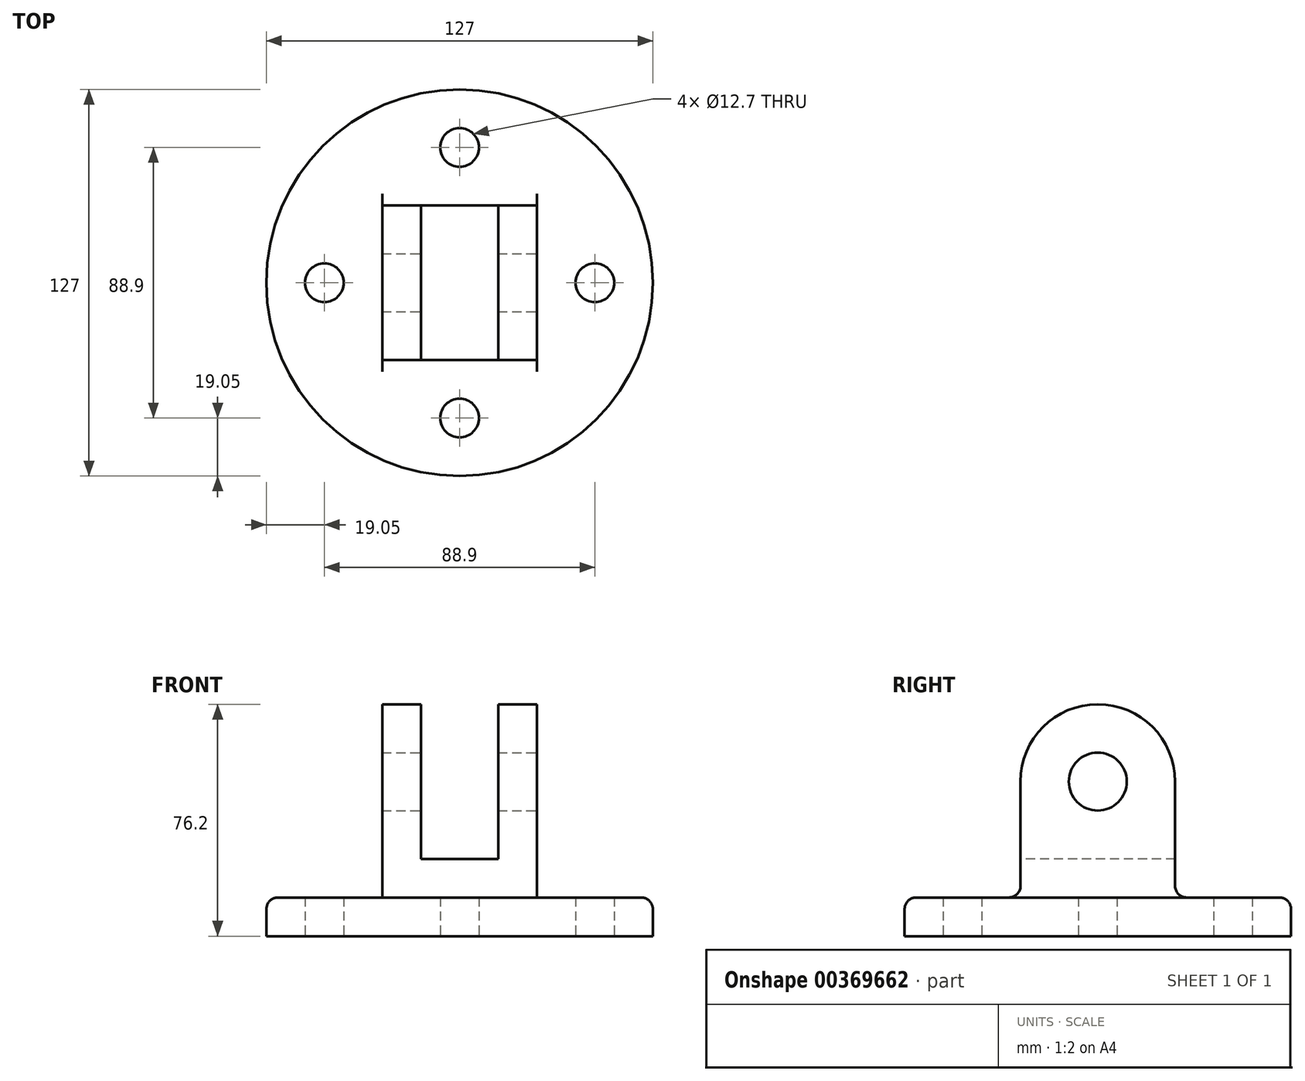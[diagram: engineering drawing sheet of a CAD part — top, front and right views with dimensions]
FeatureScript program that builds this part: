
annotation { "Feature Type Name" : "Feature", "Feature Type Description" : "" }
export const myFeature = defineFeature(function(context is Context, id is Id, definition is map)
    precondition{}
    {
        {
            var Q0;
            Q0=qCreatedBy(makeId("Top.planeOp"),FACE);
            var sketch = newSketch(context, id + "F0", { "sketchPlane" : qUnion([Q0])});
            skCircle(sketch, "E0", {"center": v(0, 0) * mm, "radius": 63.5 * mm});
            skCircle(sketch, "E1", {"center": v(0, 0) * mm, "radius": 44.45 * mm, "construction": true});
            skCircle(sketch, "E2", {"center": v(0, 44.45) * mm, "radius": 6.35 * mm});
            skCircle(sketch, "E3", {"center": v(44.45, 0) * mm, "radius": 6.35 * mm});
            skCircle(sketch, "E4", {"center": v(0, -44.45) * mm, "radius": 6.35 * mm});
            skCircle(sketch, "E5", {"center": v(-44.45, 0) * mm, "radius": 6.35 * mm});
            skLineSegment(sketch, "E6", {"start": v(-25.4, 25.4) * mm, "end": v(-25.4, -25.4) * mm});
            skLineSegment(sketch, "E7", {"start": v(-25.4, -25.4) * mm, "end": v(25.4, -25.4) * mm});
            skLineSegment(sketch, "E8", {"start": v(25.4, -25.4) * mm, "end": v(25.4, 25.4) * mm});
            skLineSegment(sketch, "E9", {"start": v(25.4, 25.4) * mm, "end": v(-25.4, 25.4) * mm});
            skLineSegment(sketch, "E10", {"start": v(-12.7, 25.4) * mm, "end": v(-12.7, -25.4) * mm});
            skLineSegment(sketch, "E11", {"start": v(12.7, 25.4) * mm, "end": v(12.7, -25.4) * mm});
            skSolve(sketch);
        }
        {
            var Q0;
            Q0=makeQuery(id+"F0.imprint","IMPRINT",FACE,{"disambiguationData":[TD([[makeQuery(id+"F0.imprint","IMPRINT",EDGE,{"derivedFrom":sQuery(id+"F0.wireOp",EDGE,"E0")}),1.0]])]});
            extrude(context, id + "F1", {"entities" : qUnion([Q0]), "depth" : 12.7 * mm});
        }
        {
            var Q0;
            {var subQ0=sQuery(id+"F0.wireOp",EDGE,"E6");Q0=makeQuery(id+"F0.imprint","IMPRINT",FACE,{"disambiguationData":[TD([[makeQuery(id+"F0.imprint","IMPRINT",EDGE,{"derivedFrom":subQ0}),1.0]])]});}
            var Q1;
            {var subQ0=sQuery(id+"F0.wireOp",EDGE,"E8");Q1=makeQuery(id+"F0.imprint","IMPRINT",FACE,{"disambiguationData":[TD([[makeQuery(id+"F0.imprint","IMPRINT",EDGE,{"derivedFrom":subQ0}),1.0]])]});}
            extrude(context, id + "F2", {"entities" : qUnion([Q0, Q1]), "operationType" : NewBodyOperationType.ADD, "depth" : 76.2 * mm});
        }
        {
            var Q0;
            {var subQ0=sQuery(id+"F0.wireOp",EDGE,"E10");Q0=makeQuery(id+"F0.imprint","IMPRINT",FACE,{"disambiguationData":[TD([[makeQuery(id+"F0.imprint","IMPRINT",EDGE,{"derivedFrom":subQ0}),1.0]])]});}
            extrude(context, id + "F3", {"entities" : qUnion([Q0]), "operationType" : NewBodyOperationType.ADD, "depth" : 25.4 * mm});
        }
        {
            var Q0;
            Q0=makeQuery(id+"F2.opExtrude","SWEPT_FACE",FACE,{"disambiguationData":[OSD([sQuery(id+"F0.wireOp",EDGE,"E8")])]});
            var sketch = newSketch(context, id + "F4", { "sketchPlane" : qUnion([Q0])});
            skLineSegment(sketch, "E12", {"start": v(0, 0) * mm, "end": v(0, 50.8) * mm, "construction": true});
            skPoint(sketch, "E12.endSnap0", {"position": v(0, 76.2) * mm});
            skCircle(sketch, "E13", {"center": v(0, 50.8) * mm, "radius": 9.53 * mm});
            skArc(sketch, "E14", {"start": v(25.4, 50.8) * mm, "mid": v(0, 76.2) * mm, "end": v(-25.4, 50.8) * mm});
            skLineSegment(sketch, "E15", {"start": v(-25.4, 12.7) * mm, "end": v(-25.4, 50.8) * mm});
            skLineSegment(sketch, "E16", {"start": v(25.4, 50.8) * mm, "end": v(25.4, 12.7) * mm});
            skLineSegment(sketch, "E17", {"start": v(-25.4, 76.2) * mm, "end": v(25.4, 76.2) * mm});
            skLineSegment(sketch, "E18", {"start": v(25.4, 76.2) * mm, "end": v(25.4, 50.8) * mm});
            skLineSegment(sketch, "E19", {"start": v(-25.4, 76.2) * mm, "end": v(-25.4, 50.8) * mm});
            skSolve(sketch);
        }
        {
            var Q0;
            Q0 = qSketchRegion(id + "F4", true);
            extrude(context, id + "F5", {"entities" : qUnion([Q0]), "operationType" : NewBodyOperationType.REMOVE, "endBound" : BoundingType.THROUGH_ALL, "oppositeDirection" : true, "depth" : 25.4 * mm});
        }
        {
            var Q0;
            Q0=makeQuery(id+"F1.opExtrude","CAP_EDGE",EDGE,{"disambiguationData":[OSD([sQuery(id+"F0.wireOp",EDGE,"E8")])],"isStart":false});
            var Q1;
            {var subQ0=sQuery(id+"F0.wireOp",EDGE,"E8");var subQ1=sQuery(id+"F0.wireOp",EDGE,"E7");var subQ2=sQuery(id+"F0.wireOp",EDGE,"E6");var subQ4=makeQuery(id+"F1.opExtrude","CAP_EDGE",EDGE,{"disambiguationData":[OSD([subQ1])],"isStart":false});Q1=makeQuery(id+"F3.boolean.opBoolean","MERGE",EDGE,{"derivedFrom":[makeQuery(id+"F2.boolean.opBoolean","SPLIT",EDGE,{"disambiguationData":[topologyDisambiguationEdgeConnected([makeQuery(id+"F2.opExtrude","SWEPT_FACE",FACE,{"disambiguationData":[OSD([subQ1]),TDD([makeQuery(id+"F0.imprint","IMPRINT",EDGE,{"disambiguationData":[TD([[makeQuery(id+"F0.imprint","INTERSECT",VERTEX,{"derivedFrom":[subQ2,subQ1]}),-1.0]])],"derivedFrom":subQ1})])]})])],"derivedFrom":subQ4}),makeQuery(id+"F2.boolean.opBoolean","SPLIT",EDGE,{"disambiguationData":[topologyDisambiguationEdgeConnected([makeQuery(id+"F2.opExtrude","SWEPT_FACE",FACE,{"disambiguationData":[OSD([subQ1]),TDD([makeQuery(id+"F0.imprint","IMPRINT",EDGE,{"disambiguationData":[TD([[makeQuery(id+"F0.imprint","INTERSECT",VERTEX,{"derivedFrom":[subQ1,subQ0]}),1.0]])],"derivedFrom":subQ1})])]})])],"derivedFrom":subQ4}),makeQuery(id+"F2.boolean.opBoolean","SPLIT",EDGE,{"disambiguationData":[topologyDisambiguationEdgeConnected([makeQuery(id+"F1.opExtrude","SWEPT_FACE",FACE,{"disambiguationData":[OSD([subQ1])]})])],"derivedFrom":subQ4})]});}
            var Q2;
            Q2=makeQuery(id+"F1.opExtrude","CAP_EDGE",EDGE,{"disambiguationData":[OSD([sQuery(id+"F0.wireOp",EDGE,"E6")])],"isStart":false});
            var Q3;
            {var subQ0=sQuery(id+"F0.wireOp",EDGE,"E9");var subQ1=sQuery(id+"F0.wireOp",EDGE,"E8");var subQ2=sQuery(id+"F0.wireOp",EDGE,"E6");var subQ4=makeQuery(id+"F1.opExtrude","CAP_EDGE",EDGE,{"disambiguationData":[OSD([subQ0])],"isStart":false});Q3=makeQuery(id+"F3.boolean.opBoolean","MERGE",EDGE,{"derivedFrom":[makeQuery(id+"F2.boolean.opBoolean","SPLIT",EDGE,{"disambiguationData":[topologyDisambiguationEdgeConnected([makeQuery(id+"F2.opExtrude","SWEPT_FACE",FACE,{"disambiguationData":[OSD([subQ0]),TDD([makeQuery(id+"F0.imprint","IMPRINT",EDGE,{"disambiguationData":[TD([[makeQuery(id+"F0.imprint","INTERSECT",VERTEX,{"derivedFrom":[subQ2,subQ0]}),1.0]])],"derivedFrom":subQ0})])]})])],"derivedFrom":subQ4}),makeQuery(id+"F2.boolean.opBoolean","SPLIT",EDGE,{"disambiguationData":[topologyDisambiguationEdgeConnected([makeQuery(id+"F2.opExtrude","SWEPT_FACE",FACE,{"disambiguationData":[OSD([subQ0]),TDD([makeQuery(id+"F0.imprint","IMPRINT",EDGE,{"disambiguationData":[TD([[makeQuery(id+"F0.imprint","INTERSECT",VERTEX,{"derivedFrom":[subQ1,subQ0]}),-1.0]])],"derivedFrom":subQ0})])]})])],"derivedFrom":subQ4}),makeQuery(id+"F2.boolean.opBoolean","SPLIT",EDGE,{"disambiguationData":[topologyDisambiguationEdgeConnected([makeQuery(id+"F1.opExtrude","SWEPT_FACE",FACE,{"disambiguationData":[OSD([subQ0])]})])],"derivedFrom":subQ4})]});}
            var Q4;
            Q4=makeQuery(id+"F1.opExtrude","CAP_EDGE",EDGE,{"disambiguationData":[OSD([sQuery(id+"F0.wireOp",EDGE,"E0")])],"isStart":false});
            fillet(context, id + "F6", {"entities" : qUnion([Q0, Q1, Q2, Q3, Q4]), "radius" : 3.8 * mm, "tangentPropagation" : true, "allowEdgeOverflow" : false});
        }
    });
